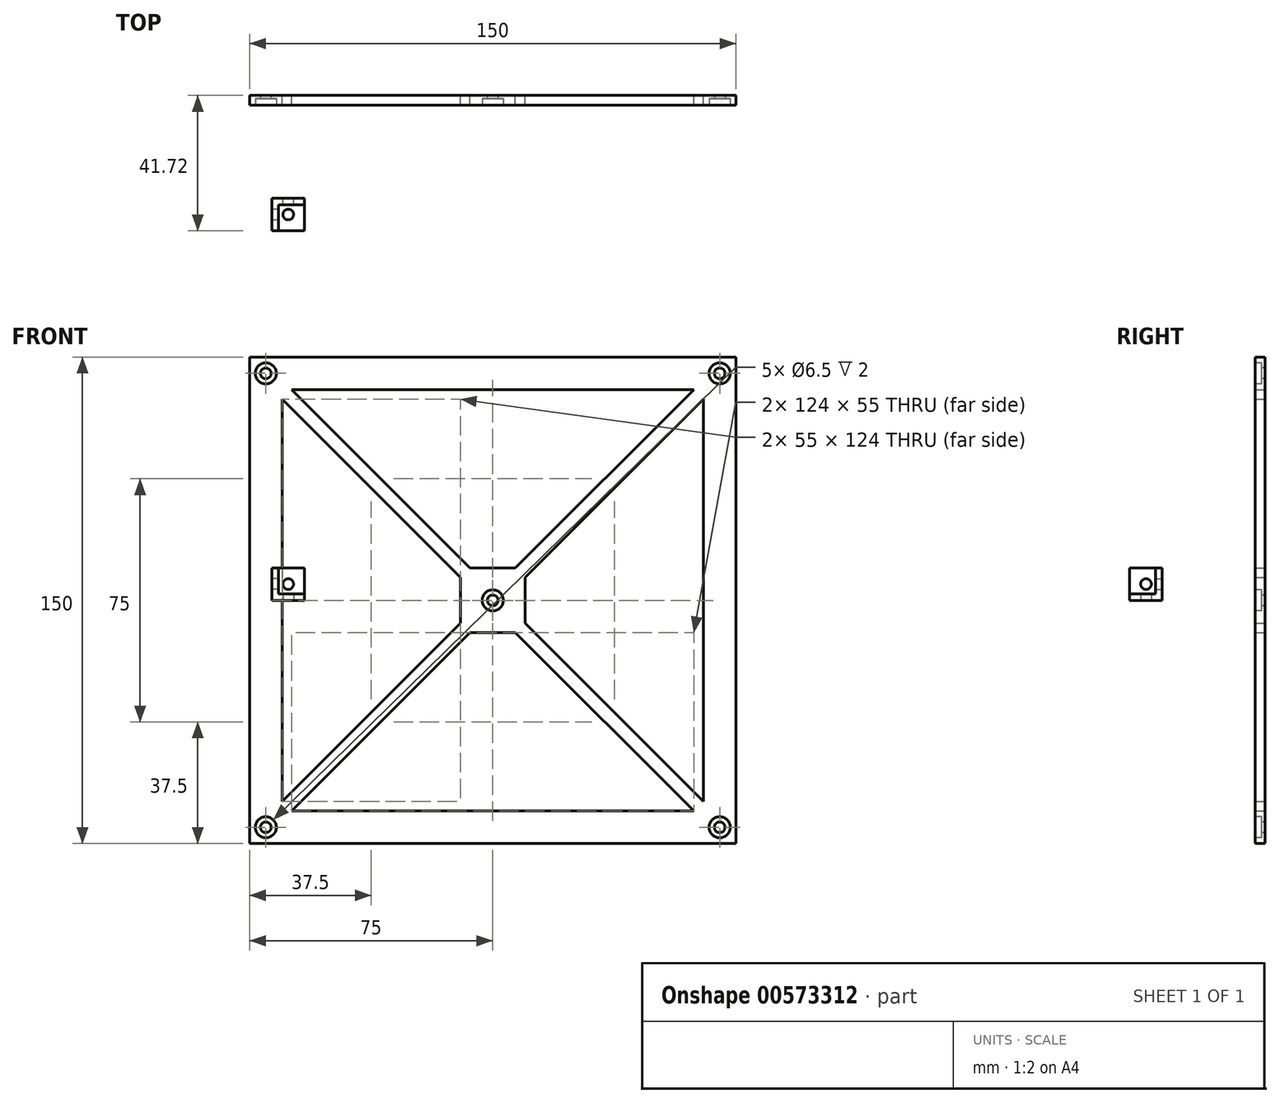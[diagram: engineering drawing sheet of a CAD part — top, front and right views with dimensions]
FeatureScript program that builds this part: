
annotation { "Feature Type Name" : "Feature", "Feature Type Description" : "" }
export const myFeature = defineFeature(function(context is Context, id is Id, definition is map)
    precondition{}
    {
        {
            var Q0;
            Q0=qCreatedBy(makeId("Front.planeOp"),FACE);
            var sketch = newSketch(context, id + "F0", { "sketchPlane" : qUnion([Q0])});
            skLineSegment(sketch, "E0.bottom", {"start": v(-75, 75) * mm, "end": v(75, 75) * mm});
            skLineSegment(sketch, "E0.top", {"start": v(-75, -75) * mm, "end": v(75, -75) * mm});
            skLineSegment(sketch, "E0.left", {"start": v(-75, 75) * mm, "end": v(-75, -75) * mm});
            skLineSegment(sketch, "E0.right", {"start": v(75, 75) * mm, "end": v(75, -75) * mm});
            skLineSegment(sketch, "E1.bottom", {"start": v(-62, 65) * mm, "end": v(62, 65) * mm});
            skLineSegment(sketch, "E1.top", {"start": v(-65, -65) * mm, "end": v(62, -65) * mm});
            skLineSegment(sketch, "E1.left", {"start": v(-65, 62) * mm, "end": v(-65, -62) * mm});
            skLineSegment(sketch, "E1.right", {"start": v(65, 62) * mm, "end": v(65, -62) * mm});
            skLineSegment(sketch, "E2.bottom", {"start": v(-7, 10) * mm, "end": v(7, 10) * mm});
            skLineSegment(sketch, "E2.top", {"start": v(-10, -10) * mm, "end": v(10, -10) * mm});
            skLineSegment(sketch, "E2.left", {"start": v(-10, 7) * mm, "end": v(-10, -10) * mm});
            skLineSegment(sketch, "E2.right", {"start": v(10, 10) * mm, "end": v(10, -10) * mm});
            skLineSegment(sketch, "E3", {"start": v(-10, 7) * mm, "end": v(-65, 62) * mm});
            skLineSegment(sketch, "E4.MirrorCS", {"start": v(-7, 10) * mm, "end": v(-62, 65) * mm});
            skLineSegment(sketch, "E5.MirrorCS", {"start": v(7, 10) * mm, "end": v(62, 65) * mm});
            skLineSegment(sketch, "E6.MirrorCS", {"start": v(10, 7) * mm, "end": v(65, 62) * mm});
            skLineSegment(sketch, "E7.MirrorCS", {"start": v(-10, -7) * mm, "end": v(-65, -62) * mm});
            skLineSegment(sketch, "E8.MirrorCS", {"start": v(-7, -10) * mm, "end": v(-62, -65) * mm});
            skLineSegment(sketch, "E9.MirrorCS", {"start": v(7, -10) * mm, "end": v(62, -65) * mm});
            skLineSegment(sketch, "E10.MirrorCS", {"start": v(10, -7) * mm, "end": v(65, -62) * mm});
            skPoint(sketch, "E11.end.orphan", {"position": v(-65, 65) * mm});
            skPoint(sketch, "E12.orphan", {"position": v(-10, 10) * mm});
            skPoint(sketch, "E13", {"position": v(0, 0) * mm});
            skSolve(sketch);
        }
        {
            var Q0;
            Q0 = qSketchRegion(id + "F0", true);
            extrude(context, id + "F1", {"entities" : qUnion([Q0]), "depth" : 3 * mm, "offsetDistance" : 25 * mm});
        }
        {
            var Q0;
            Q0=makeQuery(id+"F1.opExtrude","CAP_FACE",FACE,{"disambiguationData":[OSD([sQuery(id+"F0.wireOp",EDGE,"E0.bottom"),sQuery(id+"F0.wireOp",EDGE,"E0.top"),sQuery(id+"F0.wireOp",EDGE,"E0.left"),sQuery(id+"F0.wireOp",EDGE,"E0.right"),sQuery(id+"F0.wireOp",EDGE,"E1.bottom"),sQuery(id+"F0.wireOp",EDGE,"E1.top"),sQuery(id+"F0.wireOp",EDGE,"E1.left"),sQuery(id+"F0.wireOp",EDGE,"E1.right"),sQuery(id+"F0.wireOp",EDGE,"E2.bottom"),sQuery(id+"F0.wireOp",EDGE,"E2.top"),sQuery(id+"F0.wireOp",EDGE,"E2.left"),sQuery(id+"F0.wireOp",EDGE,"E2.right"),sQuery(id+"F0.wireOp",EDGE,"E3"),sQuery(id+"F0.wireOp",EDGE,"E4.MirrorCS"),sQuery(id+"F0.wireOp",EDGE,"E5.MirrorCS"),sQuery(id+"F0.wireOp",EDGE,"E6.MirrorCS"),sQuery(id+"F0.wireOp",EDGE,"E7.MirrorCS"),sQuery(id+"F0.wireOp",EDGE,"E8.MirrorCS"),sQuery(id+"F0.wireOp",EDGE,"E9.MirrorCS"),sQuery(id+"F0.wireOp",EDGE,"E10.MirrorCS")])],"isStart":false});
            var sketch = newSketch(context, id + "F2", { "sketchPlane" : qUnion([Q0])});
            skPoint(sketch, "E14", {"position": v(0, 0) * mm});
            skPoint(sketch, "E15", {"position": v(-70, -70) * mm});
            skPoint(sketch, "E16.MirrorP", {"position": v(-70, 70) * mm});
            skPoint(sketch, "E17.MirrorP", {"position": v(70, 70) * mm});
            skPoint(sketch, "E18.MirrorP", {"position": v(70, -70) * mm});
            skSolve(sketch);
        }
        {
            var Q0;
            Q0=sQuery(id+"F2.wireOp",VERTEX,"E14");
            var Q1;
            Q1=sQuery(id+"F2.wireOp",VERTEX,"E16.MirrorP");
            var Q2;
            Q2=sQuery(id+"F2.wireOp",VERTEX,"E17.MirrorP");
            var Q3;
            Q3=sQuery(id+"F2.wireOp",VERTEX,"E18.MirrorP");
            var Q4;
            Q4=sQuery(id+"F2.wireOp",VERTEX,"E15");
            var Q5;
            Q5=makeQuery(id+"F1.opExtrude","SWEPT_BODY",BODY,{"disambiguationData":[OSD([sQuery(id+"F0.wireOp",EDGE,"E0.bottom"),sQuery(id+"F0.wireOp",EDGE,"E0.top"),sQuery(id+"F0.wireOp",EDGE,"E0.left"),sQuery(id+"F0.wireOp",EDGE,"E0.right"),sQuery(id+"F0.wireOp",EDGE,"E1.bottom"),sQuery(id+"F0.wireOp",EDGE,"E1.top"),sQuery(id+"F0.wireOp",EDGE,"E1.left"),sQuery(id+"F0.wireOp",EDGE,"E1.right"),sQuery(id+"F0.wireOp",EDGE,"E2.bottom"),sQuery(id+"F0.wireOp",EDGE,"E2.top"),sQuery(id+"F0.wireOp",EDGE,"E2.left"),sQuery(id+"F0.wireOp",EDGE,"E2.right"),sQuery(id+"F0.wireOp",EDGE,"E3"),sQuery(id+"F0.wireOp",EDGE,"E4.MirrorCS"),sQuery(id+"F0.wireOp",EDGE,"E5.MirrorCS"),sQuery(id+"F0.wireOp",EDGE,"E6.MirrorCS"),sQuery(id+"F0.wireOp",EDGE,"E7.MirrorCS"),sQuery(id+"F0.wireOp",EDGE,"E8.MirrorCS"),sQuery(id+"F0.wireOp",EDGE,"E9.MirrorCS"),sQuery(id+"F0.wireOp",EDGE,"E10.MirrorCS")])]});
            hole(context, id + "F3", {"style" : HoleStyle.C_BORE, "endStyle" : HoleEndStyle.THROUGH, "holeDiameter" : 3.3 * mm, "cBoreDiameter" : 6.5 * mm, "cBoreDepth" : 2 * mm, "isTappedThrough" : true, "tappedDepth" : 12 * mm, "tapClearance" : 3, "startFromSketch" : true, "locations" : qUnion([Q0, Q1, Q2, Q3, Q4]), "scope" : qUnion([Q5])});
        }
        {
            var Q0;
            Q0=qCreatedBy(makeId("Top.planeOp"),FACE);
            var sketch = newSketch(context, id + "F4", { "sketchPlane" : qUnion([Q0])});
            skLineSegment(sketch, "E19.bottom", {"start": v(-68.07, -31.72) * mm, "end": v(-58.07, -31.72) * mm});
            skLineSegment(sketch, "E19.top", {"start": v(-68.07, -41.72) * mm, "end": v(-58.07, -41.72) * mm});
            skLineSegment(sketch, "E19.left", {"start": v(-68.07, -31.72) * mm, "end": v(-68.07, -41.72) * mm});
            skLineSegment(sketch, "E19.right", {"start": v(-58.07, -31.72) * mm, "end": v(-58.07, -41.72) * mm});
            skSolve(sketch);
        }
        {
            var Q0;
            Q0 = qSketchRegion(id + "F4", true);
            extrude(context, id + "F5", {"entities" : qUnion([Q0]), "depth" : 10 * mm, "offsetDistance" : 25 * mm});
        }
        {
            var Q0;
            Q0=makeQuery(id+"F5.opExtrude","SWEPT_FACE",FACE,{"disambiguationData":[OSD([sQuery(id+"F4.wireOp",EDGE,"E19.top")])]});
            var sketch = newSketch(context, id + "F6", { "sketchPlane" : qUnion([Q0])});
            skLineSegment(sketch, "E20.bottom", {"start": v(-58.07, 10) * mm, "end": v(-66.07, 10) * mm});
            skLineSegment(sketch, "E20.top", {"start": v(-58.07, 2) * mm, "end": v(-66.07, 2) * mm});
            skLineSegment(sketch, "E20.left", {"start": v(-58.07, 10) * mm, "end": v(-58.07, 2) * mm});
            skLineSegment(sketch, "E20.right", {"start": v(-66.07, 10) * mm, "end": v(-66.07, 2) * mm});
            skSolve(sketch);
        }
        {
            var Q0;
            Q0 = qSketchRegion(id + "F6", true);
            extrude(context, id + "F7", {"entities" : qUnion([Q0]), "operationType" : NewBodyOperationType.REMOVE, "oppositeDirection" : true, "depth" : 8 * mm, "offsetDistance" : 25 * mm});
        }
        {
            var Q0;
            Q0=makeQuery(id+"F5.opExtrude","SWEPT_FACE",FACE,{"disambiguationData":[OSD([sQuery(id+"F4.wireOp",EDGE,"E19.left")])]});
            var sketch = newSketch(context, id + "F8", { "sketchPlane" : qUnion([Q0])});
            skPoint(sketch, "E21", {"position": v(36.72, 5) * mm});
            skPoint(sketch, "E21.positionSnap0", {"position": v(31.72, 5) * mm});
            skPoint(sketch, "E21.positionSnap1", {"position": v(36.72, 10) * mm});
            skSolve(sketch);
        }
        {
            var Q0;
            Q0=makeQuery(id+"F5.opExtrude","CAP_FACE",FACE,{"disambiguationData":[OSD([sQuery(id+"F4.wireOp",EDGE,"E19.bottom"),sQuery(id+"F4.wireOp",EDGE,"E19.top"),sQuery(id+"F4.wireOp",EDGE,"E19.left"),sQuery(id+"F4.wireOp",EDGE,"E19.right")])],"isStart":true});
            var sketch = newSketch(context, id + "F9", { "sketchPlane" : qUnion([Q0])});
            skPoint(sketch, "E22", {"position": v(-63.07, 36.72) * mm});
            skPoint(sketch, "E22.positionSnap0", {"position": v(-63.07, 31.72) * mm});
            skPoint(sketch, "E22.positionSnap1", {"position": v(-58.07, 36.72) * mm});
            skSolve(sketch);
        }
        {
            var Q0;
            Q0=makeQuery(id+"F5.opExtrude","SWEPT_FACE",FACE,{"disambiguationData":[OSD([sQuery(id+"F4.wireOp",EDGE,"E19.bottom")])]});
            var sketch = newSketch(context, id + "F10", { "sketchPlane" : qUnion([Q0])});
            skPoint(sketch, "E23", {"position": v(63.07, 5) * mm});
            skPoint(sketch, "E23.positionSnap0", {"position": v(63.07, 0) * mm});
            skPoint(sketch, "E23.positionSnap1", {"position": v(58.07, 5) * mm});
            skSolve(sketch);
        }
        {
            var Q0;
            Q0=sQuery(id+"F10.wireOp",VERTEX,"E23");
            var Q1;
            Q1=sQuery(id+"F8.wireOp",VERTEX,"E21");
            var Q2;
            Q2=sQuery(id+"F9.wireOp",VERTEX,"E22");
            var Q3;
            Q3=makeQuery(id+"F5.opExtrude","SWEPT_BODY",BODY,{"disambiguationData":[OSD([sQuery(id+"F4.wireOp",EDGE,"E19.bottom"),sQuery(id+"F4.wireOp",EDGE,"E19.top"),sQuery(id+"F4.wireOp",EDGE,"E19.left"),sQuery(id+"F4.wireOp",EDGE,"E19.right")])]});
            hole(context, id + "F11", {"style" : HoleStyle.SIMPLE, "endStyle" : HoleEndStyle.THROUGH, "holeDiameter" : 3.3 * mm, "isTappedThrough" : true, "tappedDepth" : 12 * mm, "tapClearance" : 3, "startFromSketch" : true, "locations" : qUnion([Q0, Q1, Q2]), "scope" : qUnion([Q3])});
        }
    });
